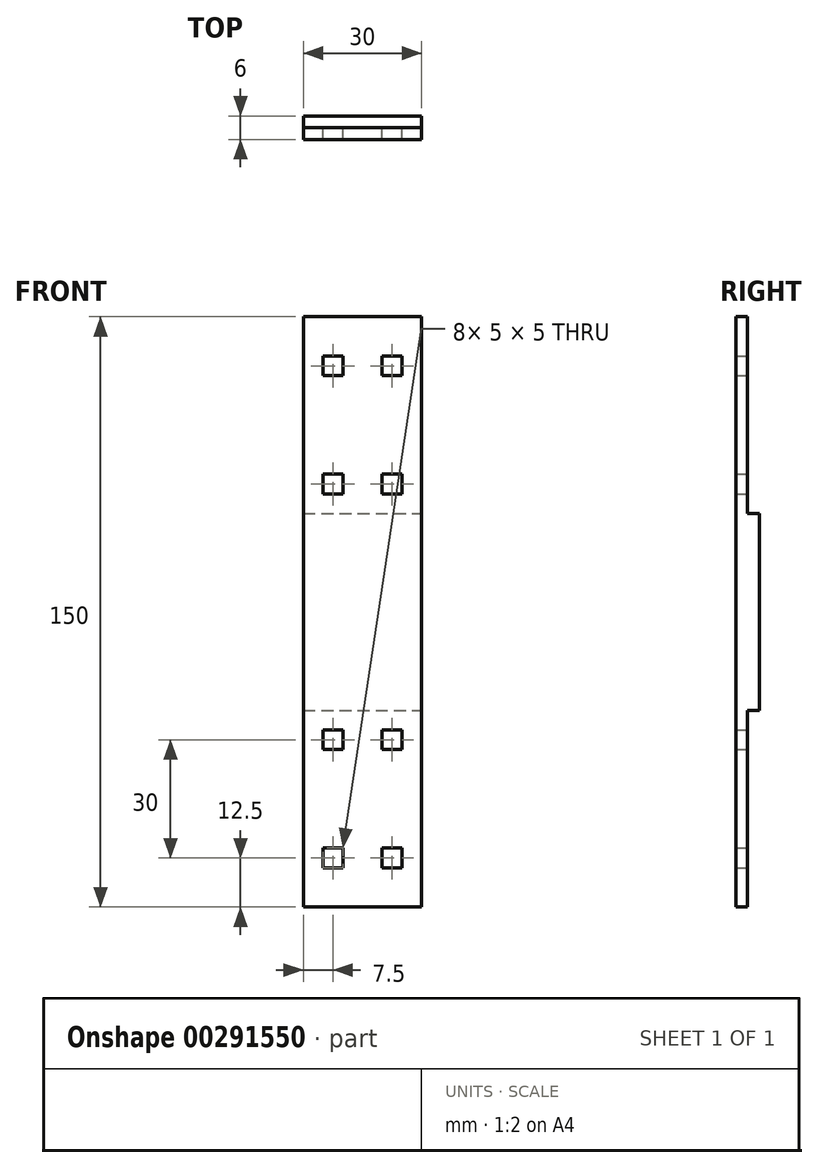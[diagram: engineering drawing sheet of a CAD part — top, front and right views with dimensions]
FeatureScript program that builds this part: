
annotation { "Feature Type Name" : "Feature", "Feature Type Description" : "" }
export const myFeature = defineFeature(function(context is Context, id is Id, definition is map)
    precondition{}
    {
        {
            var Q0;
            Q0=qCreatedBy(makeId("Top.planeOp"),FACE);
            var sketch = newSketch(context, id + "F0", { "sketchPlane" : qUnion([Q0])});
            skLineSegment(sketch, "E0.bottom", {"start": v(-15, 3) * mm, "end": v(15, 3) * mm});
            skLineSegment(sketch, "E0.top", {"start": v(-15, -3) * mm, "end": v(15, -3) * mm});
            skLineSegment(sketch, "E0.left", {"start": v(-15, 3) * mm, "end": v(-15, -3) * mm});
            skLineSegment(sketch, "E0.right", {"start": v(15, 3) * mm, "end": v(15, -3) * mm});
            skSolve(sketch);
        }
        {
            var Q0;
            Q0=qSketchRegion(id+"F0",true);
            extrude(context, id + "F1", {"entities" : qUnion([Q0]), "depth" : 150 * mm, "offsetDistance" : 25 * mm});
        }
        {
            var Q0;
            Q0=makeQuery(id+"F1.opExtrude","SWEPT_FACE",FACE,{"disambiguationData":[OSD([sQuery(id+"F0.wireOp",EDGE,"E0.right")])]});
            var sketch = newSketch(context, id + "F2", { "sketchPlane" : qUnion([Q0])});
            skLineSegment(sketch, "E1.bottom", {"start": v(0, 150) * mm, "end": v(3, 150) * mm});
            skLineSegment(sketch, "E1.top", {"start": v(0, 100) * mm, "end": v(3, 100) * mm});
            skLineSegment(sketch, "E1.left", {"start": v(0, 150) * mm, "end": v(0, 100) * mm});
            skLineSegment(sketch, "E1.right", {"start": v(3, 150) * mm, "end": v(3, 100) * mm});
            skLineSegment(sketch, "E2.MirrorCS", {"start": v(0, 0) * mm, "end": v(3, 0) * mm});
            skLineSegment(sketch, "E3.MirrorCS", {"start": v(0, 50) * mm, "end": v(3, 50) * mm});
            skLineSegment(sketch, "E4.MirrorCS", {"start": v(0, 0) * mm, "end": v(0, 50) * mm});
            skLineSegment(sketch, "E5.MirrorCS", {"start": v(3, 0) * mm, "end": v(3, 50) * mm});
            skSolve(sketch);
        }
        {
            var Q0;
            Q0 = qSketchRegion(id + "F2", true);
            extrude(context, id + "F3", {"entities" : qUnion([Q0]), "operationType" : NewBodyOperationType.REMOVE, "endBound" : BoundingType.UP_TO_NEXT, "oppositeDirection" : true, "depth" : 25 * mm, "offsetDistance" : 25 * mm});
        }
        {
            var Q0;
            Q0=makeQuery(id+"F3.boolean.opBoolean","COPY",FACE,{"derivedFrom":makeQuery(id+"F3.opExtrude","SWEPT_FACE",FACE,{"disambiguationData":[OSD([sQuery(id+"F2.wireOp",EDGE,"E1.left")])]})});
            var sketch = newSketch(context, id + "F4", { "sketchPlane" : qUnion([Q0])});
            skLineSegment(sketch, "E6.bottom", {"start": v(5, 15) * mm, "end": v(10, 15) * mm});
            skLineSegment(sketch, "E6.top", {"start": v(5, 10) * mm, "end": v(10, 10) * mm});
            skLineSegment(sketch, "E6.left", {"start": v(5, 15) * mm, "end": v(5, 10) * mm});
            skLineSegment(sketch, "E6.right", {"start": v(10, 15) * mm, "end": v(10, 10) * mm});
            skLineSegment(sketch, "E7.MirrorCS", {"start": v(-5, 10) * mm, "end": v(-10, 10) * mm});
            skLineSegment(sketch, "E8.MirrorCS", {"start": v(-5, 15) * mm, "end": v(-5, 10) * mm});
            skLineSegment(sketch, "E9.MirrorCS", {"start": v(-10, 15) * mm, "end": v(-10, 10) * mm});
            skLineSegment(sketch, "E10.MirrorCS", {"start": v(-5, 15) * mm, "end": v(-10, 15) * mm});
            skLineSegment(sketch, "E11.MirrorCS", {"start": v(-5, 40) * mm, "end": v(-5, 45) * mm});
            skLineSegment(sketch, "E12.MirrorCS", {"start": v(-5, 45) * mm, "end": v(-10, 45) * mm});
            skLineSegment(sketch, "E13.MirrorCS", {"start": v(5, 40) * mm, "end": v(10, 40) * mm});
            skLineSegment(sketch, "E14.MirrorCS", {"start": v(5, 45) * mm, "end": v(10, 45) * mm});
            skLineSegment(sketch, "E15.MirrorCS", {"start": v(5, 40) * mm, "end": v(5, 45) * mm});
            skLineSegment(sketch, "E16.MirrorCS", {"start": v(10, 40) * mm, "end": v(10, 45) * mm});
            skLineSegment(sketch, "E17.MirrorCS", {"start": v(-5, 40) * mm, "end": v(-10, 40) * mm});
            skLineSegment(sketch, "E18.MirrorCS", {"start": v(-10, 40) * mm, "end": v(-10, 45) * mm});
            skLineSegment(sketch, "E19.MirrorCS", {"start": v(5, 110) * mm, "end": v(5, 105) * mm});
            skLineSegment(sketch, "E20.MirrorCS", {"start": v(5, 105) * mm, "end": v(10, 105) * mm});
            skLineSegment(sketch, "E21.MirrorCS", {"start": v(5, 110) * mm, "end": v(10, 110) * mm});
            skLineSegment(sketch, "E22.MirrorCS", {"start": v(-5, 105) * mm, "end": v(-10, 105) * mm});
            skLineSegment(sketch, "E23.MirrorCS", {"start": v(-5, 110) * mm, "end": v(-5, 105) * mm});
            skLineSegment(sketch, "E24.MirrorCS", {"start": v(-10, 110) * mm, "end": v(-10, 105) * mm});
            skLineSegment(sketch, "E25.MirrorCS", {"start": v(-5, 135) * mm, "end": v(-10, 135) * mm});
            skLineSegment(sketch, "E26.MirrorCS", {"start": v(-5, 140) * mm, "end": v(-10, 140) * mm});
            skLineSegment(sketch, "E27.MirrorCS", {"start": v(10, 135) * mm, "end": v(10, 140) * mm});
            skLineSegment(sketch, "E28.MirrorCS", {"start": v(5, 135) * mm, "end": v(5, 140) * mm});
            skLineSegment(sketch, "E29.MirrorCS", {"start": v(10, 110) * mm, "end": v(10, 105) * mm});
            skLineSegment(sketch, "E30.MirrorCS", {"start": v(5, 135) * mm, "end": v(10, 135) * mm});
            skLineSegment(sketch, "E31.MirrorCS", {"start": v(-5, 110) * mm, "end": v(-10, 110) * mm});
            skLineSegment(sketch, "E32.MirrorCS", {"start": v(-10, 135) * mm, "end": v(-10, 140) * mm});
            skLineSegment(sketch, "E33.MirrorCS", {"start": v(-5, 135) * mm, "end": v(-5, 140) * mm});
            skLineSegment(sketch, "E34.MirrorCS", {"start": v(5, 140) * mm, "end": v(10, 140) * mm});
            skSolve(sketch);
        }
        {
            var Q0;
            Q0 = qSketchRegion(id + "F4", true);
            extrude(context, id + "F5", {"entities" : qUnion([Q0]), "operationType" : NewBodyOperationType.REMOVE, "endBound" : BoundingType.UP_TO_NEXT, "oppositeDirection" : true, "depth" : 25 * mm, "offsetDistance" : 25 * mm});
        }
    });
